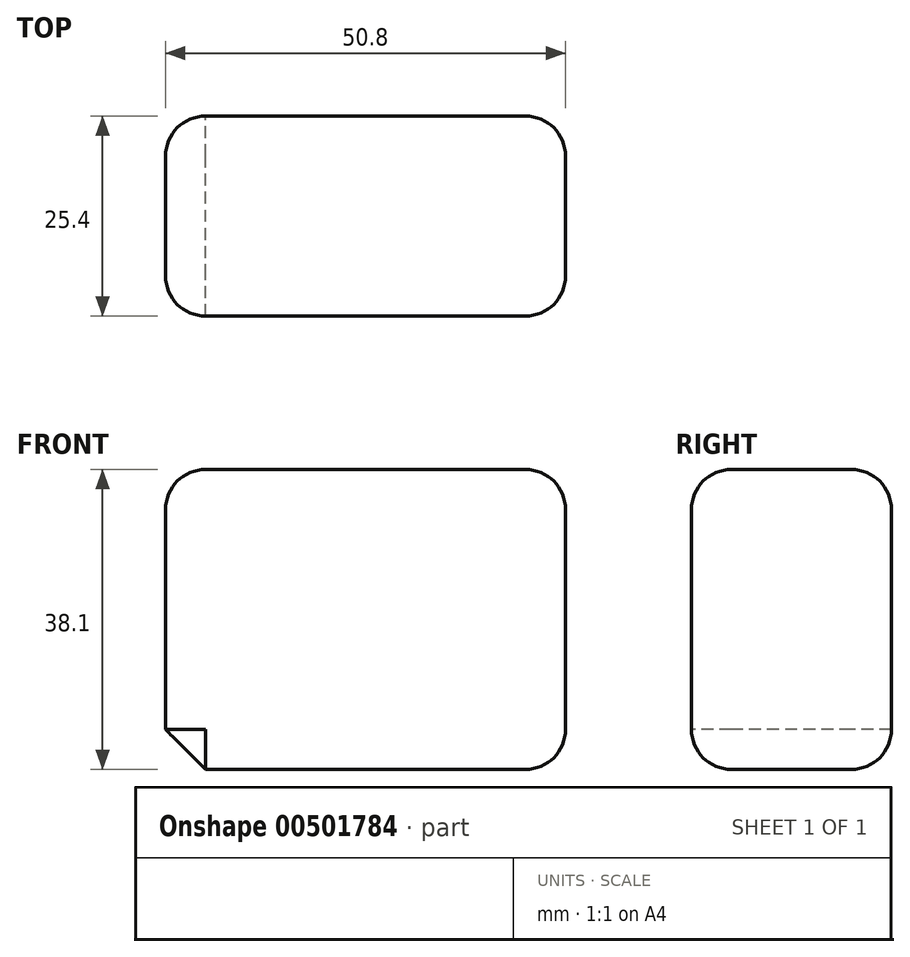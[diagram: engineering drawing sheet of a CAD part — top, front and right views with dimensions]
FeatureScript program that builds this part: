
annotation { "Feature Type Name" : "Feature", "Feature Type Description" : "" }
export const myFeature = defineFeature(function(context is Context, id is Id, definition is map)
    precondition{}
    {
        {
            var Q0;
            Q0=qCreatedBy(makeId("Front.planeOp"),FACE);
            var sketch = newSketch(context, id + "F0", { "sketchPlane" : qUnion([Q0])});
            skLineSegment(sketch, "E0", {"start": v(0, 0) * mm, "end": v(50.8, 0) * mm});
            skLineSegment(sketch, "E1", {"start": v(50.8, 0) * mm, "end": v(50.8, 38.1) * mm});
            skLineSegment(sketch, "E2", {"start": v(50.8, 38.1) * mm, "end": v(0, 38.1) * mm});
            skLineSegment(sketch, "E3", {"start": v(0, 38.1) * mm, "end": v(0, 0) * mm});
            skSolve(sketch);
        }
        {
            var Q0;
            Q0=makeQuery(id+"F0.imprint","IMPRINT",FACE,{"disambiguationData":[TD([[makeQuery(id+"F0.imprint","IMPRINT",EDGE,{"derivedFrom":sQuery(id+"F0.wireOp",EDGE,"E0")}),1.0]])]});
            extrude(context, id + "F1", {"entities" : qUnion([Q0]), "endBound" : BoundingType.SYMMETRIC, "depth" : 25.4 * mm});
        }
        {
            var Q0;
            Q0=makeQuery(id+"F1.opExtrude","CAP_EDGE",EDGE,{"disambiguationData":[OSD([sQuery(id+"F0.wireOp",EDGE,"E2")])],"isStart":false});
            var Q1;
            Q1=makeQuery(id+"F1.opExtrude","SWEPT_FACE",FACE,{"disambiguationData":[OSD([sQuery(id+"F0.wireOp",EDGE,"E2")])]});
            var Q2;
            Q2=makeQuery(id+"F1.opExtrude","CAP_EDGE",EDGE,{"disambiguationData":[OSD([sQuery(id+"F0.wireOp",EDGE,"E1")])],"isStart":false});
            var Q3;
            Q3=makeQuery(id+"F1.opExtrude","CAP_EDGE",EDGE,{"disambiguationData":[OSD([sQuery(id+"F0.wireOp",EDGE,"E1")])],"isStart":true});
            var Q4;
            Q4=makeQuery(id+"F1.opExtrude","SWEPT_EDGE",EDGE,{"disambiguationData":[OSD([sQuery(id+"F0.wireOp",EDGE,"E0"),sQuery(id+"F0.wireOp",EDGE,"E1")])]});
            var Q5;
            Q5=makeQuery(id+"F1.opExtrude","CAP_EDGE",EDGE,{"disambiguationData":[OSD([sQuery(id+"F0.wireOp",EDGE,"E0")])],"isStart":false});
            var Q6;
            Q6=makeQuery(id+"F1.opExtrude","CAP_EDGE",EDGE,{"disambiguationData":[OSD([sQuery(id+"F0.wireOp",EDGE,"E3")])],"isStart":false});
            var Q7;
            Q7=makeQuery(id+"F1.opExtrude","CAP_EDGE",EDGE,{"disambiguationData":[OSD([sQuery(id+"F0.wireOp",EDGE,"E3")])],"isStart":true});
            var Q8;
            Q8=makeQuery(id+"F1.opExtrude","CAP_EDGE",EDGE,{"disambiguationData":[OSD([sQuery(id+"F0.wireOp",EDGE,"E0")])],"isStart":true});
            fillet(context, id + "F2", {"entities" : qUnion([Q0, Q1, Q2, Q3, Q4, Q5, Q6, Q7, Q8]), "radius" : 5.08 * mm, "tangentPropagation" : true, "allowEdgeOverflow" : false});
        }
        {
            var Q0;
            Q0=makeQuery(id+"F2.opFillet","BLEND_EDGE",EDGE,{"blendedFrom":[makeQuery(id+"F1.opExtrude","CAP_EDGE",EDGE,{"disambiguationData":[OSD([sQuery(id+"F0.wireOp",EDGE,"E0")])],"isStart":false}),makeQuery(id+"F1.opExtrude","CAP_EDGE",EDGE,{"disambiguationData":[OSD([sQuery(id+"F0.wireOp",EDGE,"E3")])],"isStart":false})],"blendedInto":[]});
            chamfer(context, id + "F3", {"entities" : qUnion([Q0]), "width" : 5.08 * mm, "tangentPropagation" : true});
        }
    });
